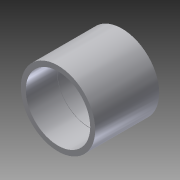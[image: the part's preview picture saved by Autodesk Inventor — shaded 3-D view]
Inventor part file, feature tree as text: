
AUTODESK INVENTOR PART (.ipt)
format: ipt  version: 2014 (Build 180170000, 170)  size: 106,496 bytes
history: native  units: in
note: dims shown in document units (in); Inventor stores cm internally (conversion verified against a paired STEP export)
features: extrude x3, sketch x3
ambient origin geometry x8: Origin, YZ Plane, XZ Plane, XY Plane, X Axis, Y Axis, Z Axis, Center Point
bodies: Solid1 (feature_tree)
feature tree (6):
  extrude  "Extrusion1"  Depth=0.2in
  extrude  "Extrusion2"  Depth=2.375in
  extrude  "Extrusion3"  Depth=1.156in
  sketch  "Sketch1"  dims[d0=2.36in d1=0.2in]
  sketch  "Sketch3"  dims[d2=2.375in d3=0.0in d4=2.39in]
  sketch  "Sketch4"  dims[d5=1.156in d6=0.0in d7=2.39in d8=1.156in d9=0.0in]
